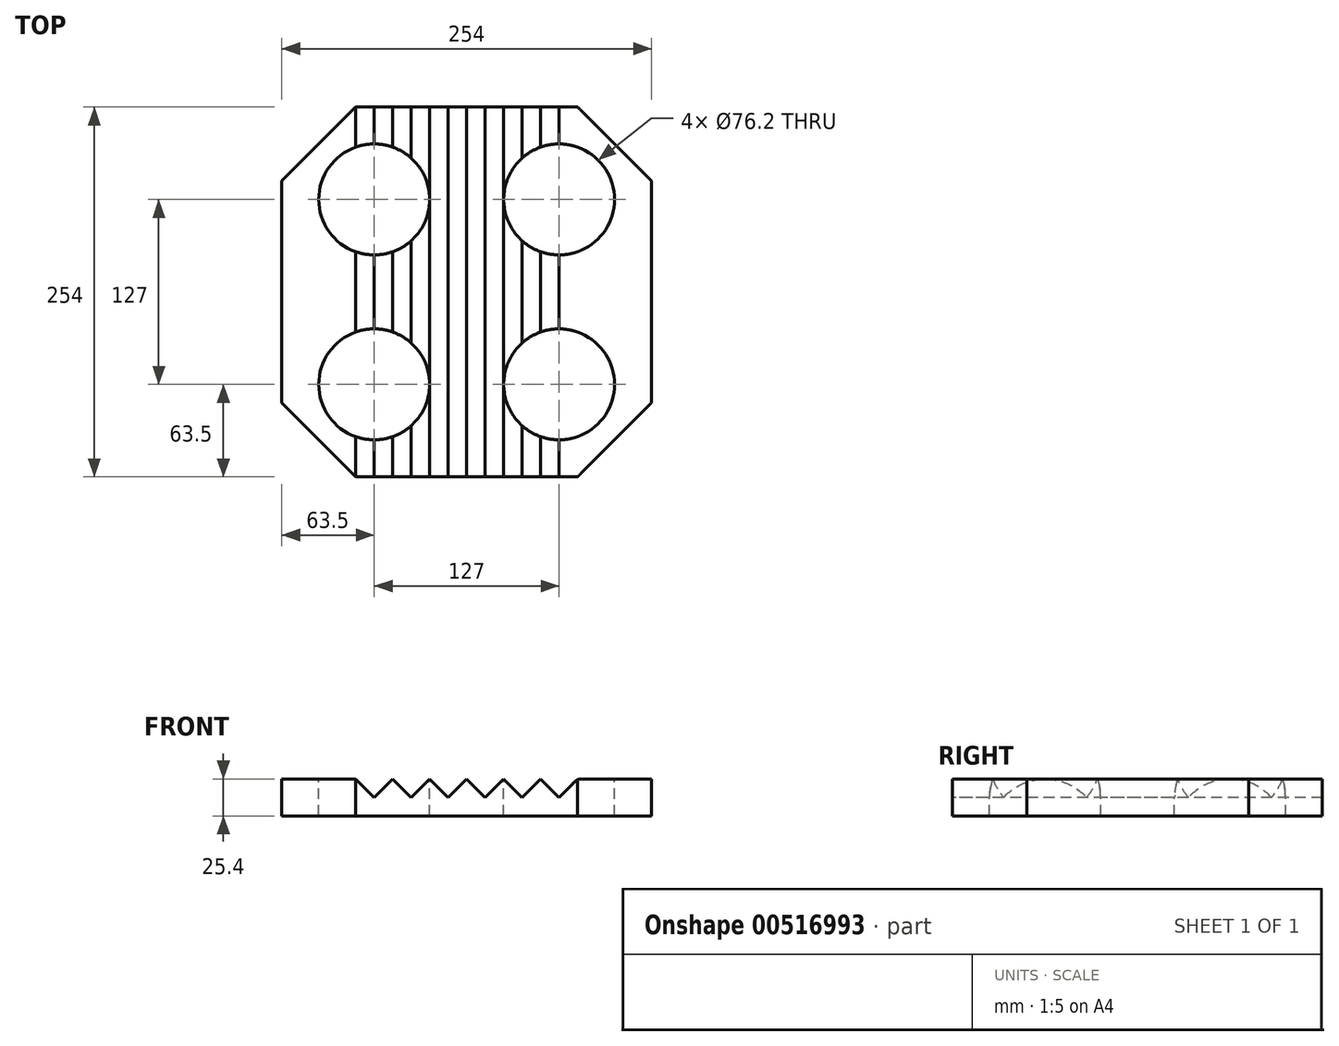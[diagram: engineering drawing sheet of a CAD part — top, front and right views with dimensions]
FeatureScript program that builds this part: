
annotation { "Feature Type Name" : "Feature", "Feature Type Description" : "" }
export const myFeature = defineFeature(function(context is Context, id is Id, definition is map)
    precondition{}
    {
        {
            var Q0;
            Q0=qCreatedBy(makeId("Top.planeOp"),FACE);
            var sketch = newSketch(context, id + "F0", { "sketchPlane" : qUnion([Q0])});
            skLineSegment(sketch, "E0.bottom", {"start": v(-127, 127) * mm, "end": v(127, 127) * mm});
            skLineSegment(sketch, "E0.top", {"start": v(-127, -127) * mm, "end": v(127, -127) * mm});
            skLineSegment(sketch, "E0.left", {"start": v(-127, 127) * mm, "end": v(-127, -127) * mm});
            skLineSegment(sketch, "E0.right", {"start": v(127, 127) * mm, "end": v(127, -127) * mm});
            skLineSegment(sketch, "E1", {"start": v(-127, 127) * mm, "end": v(127, -127) * mm, "construction": true});
            skLineSegment(sketch, "E2", {"start": v(127, 127) * mm, "end": v(-127, -127) * mm, "construction": true});
            skSolve(sketch);
        }
        {
            var Q0;
            Q0 = qSketchRegion(id + "F0", true);
            extrude(context, id + "F1", {"entities" : qUnion([Q0]), "depth" : 25.4 * mm, "offsetDistance" : 25.4 * mm});
        }
        {
            var Q0;
            Q0=makeQuery(id+"F1.opExtrude","CAP_FACE",FACE,{"disambiguationData":[OSD([sQuery(id+"F0.wireOp",EDGE,"E0.bottom"),sQuery(id+"F0.wireOp",EDGE,"E0.top"),sQuery(id+"F0.wireOp",EDGE,"E0.left"),sQuery(id+"F0.wireOp",EDGE,"E0.right")])],"isStart":false});
            var sketch = newSketch(context, id + "F2", { "sketchPlane" : qUnion([Q0])});
            skPoint(sketch, "E3", {"position": v(-63.5, 63.5) * mm});
            skPoint(sketch, "E4", {"position": v(63.5, 63.5) * mm});
            skPoint(sketch, "E5", {"position": v(63.5, -63.5) * mm});
            skPoint(sketch, "E6", {"position": v(-63.5, -63.5) * mm});
            skLineSegment(sketch, "E7", {"start": v(-63.5, 63.5) * mm, "end": v(-63.5, -63.5) * mm, "construction": true});
            skLineSegment(sketch, "E8", {"start": v(63.5, -63.5) * mm, "end": v(63.5, 63.5) * mm, "construction": true});
            skLineSegment(sketch, "E9", {"start": v(63.5, 63.5) * mm, "end": v(-63.5, 63.5) * mm, "construction": true});
            skLineSegment(sketch, "E10", {"start": v(63.5, -63.5) * mm, "end": v(-63.5, -63.5) * mm, "construction": true});
            skSolve(sketch);
        }
        {
            var Q0;
            Q0=sQuery(id+"F2.wireOp",VERTEX,"E3");
            var Q1;
            Q1=sQuery(id+"F2.wireOp",VERTEX,"E4");
            var Q2;
            Q2=sQuery(id+"F2.wireOp",VERTEX,"E5");
            var Q3;
            Q3=sQuery(id+"F2.wireOp",VERTEX,"E6");
            var Q4;
            Q4=makeQuery(id+"F1.opExtrude","SWEPT_BODY",BODY,{"disambiguationData":[OSD([sQuery(id+"F0.wireOp",EDGE,"E0.bottom"),sQuery(id+"F0.wireOp",EDGE,"E0.top"),sQuery(id+"F0.wireOp",EDGE,"E0.left"),sQuery(id+"F0.wireOp",EDGE,"E0.right")])]});
            hole(context, id + "F3", {"style" : HoleStyle.SIMPLE, "endStyle" : HoleEndStyle.THROUGH, "holeDiameter" : 76.2 * mm, "isTappedThrough" : true, "tappedDepth" : 12.7 * mm, "tapClearance" : 3, "locations" : qUnion([Q0, Q1, Q2, Q3]), "scope" : qUnion([Q4])});
        }
        {
            var Q0;
            Q0=makeQuery(id+"F1.opExtrude","SWEPT_EDGE",EDGE,{"disambiguationData":[OSD([sQuery(id+"F0.wireOp",EDGE,"E0.bottom"),sQuery(id+"F0.wireOp",EDGE,"E0.right")])]});
            var Q1;
            Q1=makeQuery(id+"F1.opExtrude","SWEPT_EDGE",EDGE,{"disambiguationData":[OSD([sQuery(id+"F0.wireOp",EDGE,"E0.top"),sQuery(id+"F0.wireOp",EDGE,"E0.right")])]});
            var Q2;
            Q2=makeQuery(id+"F1.opExtrude","SWEPT_EDGE",EDGE,{"disambiguationData":[OSD([sQuery(id+"F0.wireOp",EDGE,"E0.top"),sQuery(id+"F0.wireOp",EDGE,"E0.left")])]});
            var Q3;
            Q3=makeQuery(id+"F1.opExtrude","SWEPT_EDGE",EDGE,{"disambiguationData":[OSD([sQuery(id+"F0.wireOp",EDGE,"E0.bottom"),sQuery(id+"F0.wireOp",EDGE,"E0.left")])]});
            chamfer(context, id + "F4", {"entities" : qUnion([Q0, Q1, Q2, Q3]), "width" : 50.8 * mm, "tangentPropagation" : true});
        }
        {
            var Q0;
            Q0=makeQuery(id+"F1.opExtrude","SWEPT_FACE",FACE,{"disambiguationData":[OSD([sQuery(id+"F0.wireOp",EDGE,"E0.top")])]});
            var sketch = newSketch(context, id + "F5", { "sketchPlane" : qUnion([Q0])});
            skLineSegment(sketch, "E11", {"start": v(-76.2, 12.7) * mm, "end": v(76.2, 12.7) * mm, "construction": true});
            skLineSegment(sketch, "E12", {"start": v(-76.2, 25.4) * mm, "end": v(-63.5, 12.7) * mm});
            skLineSegment(sketch, "E13", {"start": v(-63.5, 12.7) * mm, "end": v(-50.8, 25.4) * mm});
            skLineSegment(sketch, "E14", {"start": v(-50.8, 25.4) * mm, "end": v(-38.1, 12.7) * mm});
            skLineSegment(sketch, "E15", {"start": v(-38.1, 12.7) * mm, "end": v(-25.4, 25.4) * mm});
            skLineSegment(sketch, "E16", {"start": v(-25.4, 25.4) * mm, "end": v(-12.7, 12.7) * mm});
            skLineSegment(sketch, "E17", {"start": v(-12.7, 12.7) * mm, "end": v(0, 25.4) * mm});
            skLineSegment(sketch, "E18", {"start": v(0, 25.4) * mm, "end": v(12.7, 12.7) * mm});
            skLineSegment(sketch, "E19", {"start": v(12.7, 12.7) * mm, "end": v(25.4, 25.4) * mm});
            skLineSegment(sketch, "E20", {"start": v(25.4, 25.4) * mm, "end": v(38.1, 12.7) * mm});
            skLineSegment(sketch, "E21", {"start": v(38.1, 12.7) * mm, "end": v(50.8, 25.4) * mm});
            skLineSegment(sketch, "E22", {"start": v(50.8, 25.4) * mm, "end": v(63.5, 12.7) * mm});
            skLineSegment(sketch, "E23", {"start": v(63.5, 12.7) * mm, "end": v(76.2, 25.4) * mm});
            skLineSegment(sketch, "E24", {"start": v(-76.2, 25.4) * mm, "end": v(76.2, 25.4) * mm});
            skSolve(sketch);
        }
        {
            var Q0;
            {var subQ0=sQuery(id+"F5.wireOp",EDGE,"E12");Q0=makeQuery(id+"F5.imprint","IMPRINT",FACE,{"disambiguationData":[TD([[makeQuery(id+"F5.imprint","IMPRINT",EDGE,{"derivedFrom":subQ0}),1.0]])]});}
            var Q1;
            {var subQ0=sQuery(id+"F5.wireOp",EDGE,"E14");Q1=makeQuery(id+"F5.imprint","IMPRINT",FACE,{"disambiguationData":[TD([[makeQuery(id+"F5.imprint","IMPRINT",EDGE,{"derivedFrom":subQ0}),1.0]])]});}
            var Q2;
            {var subQ0=sQuery(id+"F5.wireOp",EDGE,"E16");Q2=makeQuery(id+"F5.imprint","IMPRINT",FACE,{"disambiguationData":[TD([[makeQuery(id+"F5.imprint","IMPRINT",EDGE,{"derivedFrom":subQ0}),1.0]])]});}
            var Q3;
            {var subQ0=sQuery(id+"F5.wireOp",EDGE,"E18");Q3=makeQuery(id+"F5.imprint","IMPRINT",FACE,{"disambiguationData":[TD([[makeQuery(id+"F5.imprint","IMPRINT",EDGE,{"derivedFrom":subQ0}),1.0]])]});}
            var Q4;
            {var subQ0=sQuery(id+"F5.wireOp",EDGE,"E20");Q4=makeQuery(id+"F5.imprint","IMPRINT",FACE,{"disambiguationData":[TD([[makeQuery(id+"F5.imprint","IMPRINT",EDGE,{"derivedFrom":subQ0}),1.0]])]});}
            var Q5;
            {var subQ0=sQuery(id+"F5.wireOp",EDGE,"E22");Q5=makeQuery(id+"F5.imprint","IMPRINT",FACE,{"disambiguationData":[TD([[makeQuery(id+"F5.imprint","IMPRINT",EDGE,{"derivedFrom":subQ0}),1.0]])]});}
            extrude(context, id + "F6", {"entities" : qUnion([Q0, Q1, Q2, Q3, Q4, Q5]), "operationType" : NewBodyOperationType.REMOVE, "endBound" : BoundingType.THROUGH_ALL, "oppositeDirection" : true, "depth" : 25.4 * mm, "offsetDistance" : 25.4 * mm});
        }
        {
            var Q0;
            {var subQ0=sQuery(id+"F0.wireOp",EDGE,"E0.left");var subQ1=sQuery(id+"F0.wireOp",EDGE,"E0.top");var subQ2=sQuery(id+"F5.wireOp",EDGE,"E12");Q0=makeQuery(id+"F6.boolean.opBoolean","COPY",EDGE,{"disambiguationData":[TD([makeQuery(id+"F1.opExtrude","CAP_FACE",FACE,{"disambiguationData":[OSD([sQuery(id+"F0.wireOp",EDGE,"E0.bottom"),subQ1,subQ0,sQuery(id+"F0.wireOp",EDGE,"E0.right")])],"isStart":false}),makeQuery(id+"F1.opExtrude","SWEPT_FACE",FACE,{"disambiguationData":[OSD([subQ1])]}),makeQuery(id+"F3.hole-3.boolean.opBoolean","COPY",FACE,{"derivedFrom":makeQuery(id+"F3.hole-3.opRevolve","SWEPT_FACE",FACE,{"disambiguationData":[OSD([sQuery(id+"F3.hole-3.sketch.wireOp",EDGE,"core_line_2")])]})}),makeQuery(id+"F4.opChamfer","BLEND_FACE",FACE,{"disambiguationData":[OSD([subQ1,subQ0])]}),makeQuery(id+"F6.opExtrude","SWEPT_FACE",FACE,{"disambiguationData":[OSD([subQ2])]})])],"derivedFrom":makeQuery(id+"F6.opExtrude","SWEPT_EDGE",EDGE,{"disambiguationData":[OSD([subQ1,subQ0,subQ2,sQuery(id+"F5.wireOp",EDGE,"E24")])]})});}
            var Q1;
            {var subQ0=sQuery(id+"F5.wireOp",EDGE,"E24");var subQ1=sQuery(id+"F5.wireOp",EDGE,"E14");var subQ2=sQuery(id+"F5.wireOp",EDGE,"E13");Q1=makeQuery(id+"F6.boolean.opBoolean","TWEAK_EDGE",EDGE,{"disambiguationData":[OD(0.0)],"derivedFrom":[makeQuery(id+"F6.opExtrude","SWEPT_EDGE",EDGE,{"disambiguationData":[OSD([subQ2,subQ1,subQ0]),OD(0.0)]}),makeQuery(id+"F6.opExtrude","SWEPT_EDGE",EDGE,{"disambiguationData":[OSD([subQ2,subQ1,subQ0]),OD(1.0)]})]});}
            var Q2;
            {var subQ0=sQuery(id+"F5.wireOp",EDGE,"E24");var subQ1=sQuery(id+"F5.wireOp",EDGE,"E14");var subQ2=sQuery(id+"F5.wireOp",EDGE,"E13");Q2=makeQuery(id+"F6.boolean.opBoolean","TWEAK_EDGE",EDGE,{"disambiguationData":[OD(1.0)],"derivedFrom":[makeQuery(id+"F6.opExtrude","SWEPT_EDGE",EDGE,{"disambiguationData":[OSD([subQ2,subQ1,subQ0]),OD(0.0)]}),makeQuery(id+"F6.opExtrude","SWEPT_EDGE",EDGE,{"disambiguationData":[OSD([subQ2,subQ1,subQ0]),OD(1.0)]})]});}
            var Q3;
            {var subQ0=sQuery(id+"F5.wireOp",EDGE,"E24");var subQ1=sQuery(id+"F5.wireOp",EDGE,"E16");var subQ2=sQuery(id+"F5.wireOp",EDGE,"E15");Q3=makeQuery(id+"F6.boolean.opBoolean","TWEAK_EDGE",EDGE,{"disambiguationData":[OD(2.0)],"derivedFrom":[makeQuery(id+"F6.opExtrude","SWEPT_EDGE",EDGE,{"disambiguationData":[OSD([subQ2,subQ1,subQ0]),OD(0.0)]}),makeQuery(id+"F6.opExtrude","SWEPT_EDGE",EDGE,{"disambiguationData":[OSD([subQ2,subQ1,subQ0]),OD(1.0)]})]});}
            var Q4;
            {var subQ0=sQuery(id+"F5.wireOp",EDGE,"E24");var subQ1=sQuery(id+"F5.wireOp",EDGE,"E16");var subQ2=sQuery(id+"F5.wireOp",EDGE,"E15");Q4=makeQuery(id+"F6.boolean.opBoolean","TWEAK_EDGE",EDGE,{"disambiguationData":[OD(0.0)],"derivedFrom":[makeQuery(id+"F6.opExtrude","SWEPT_EDGE",EDGE,{"disambiguationData":[OSD([subQ2,subQ1,subQ0]),OD(0.0)]}),makeQuery(id+"F6.opExtrude","SWEPT_EDGE",EDGE,{"disambiguationData":[OSD([subQ2,subQ1,subQ0]),OD(1.0)]})]});}
            var Q5;
            {var subQ0=sQuery(id+"F5.wireOp",EDGE,"E24");var subQ1=sQuery(id+"F5.wireOp",EDGE,"E18");var subQ2=sQuery(id+"F5.wireOp",EDGE,"E17");Q5=makeQuery(id+"F6.boolean.opBoolean","TWEAK_EDGE",EDGE,{"derivedFrom":[makeQuery(id+"F6.opExtrude","SWEPT_EDGE",EDGE,{"disambiguationData":[OSD([subQ2,subQ1,subQ0]),OD(0.0)]}),makeQuery(id+"F6.opExtrude","SWEPT_EDGE",EDGE,{"disambiguationData":[OSD([subQ2,subQ1,subQ0]),OD(1.0)]})]});}
            var Q6;
            {var subQ0=sQuery(id+"F5.wireOp",EDGE,"E24");var subQ1=sQuery(id+"F5.wireOp",EDGE,"E20");var subQ2=sQuery(id+"F5.wireOp",EDGE,"E19");Q6=makeQuery(id+"F6.boolean.opBoolean","TWEAK_EDGE",EDGE,{"disambiguationData":[OD(0.0)],"derivedFrom":[makeQuery(id+"F6.opExtrude","SWEPT_EDGE",EDGE,{"disambiguationData":[OSD([subQ2,subQ1,subQ0]),OD(0.0)]}),makeQuery(id+"F6.opExtrude","SWEPT_EDGE",EDGE,{"disambiguationData":[OSD([subQ2,subQ1,subQ0]),OD(1.0)]})]});}
            var Q7;
            {var subQ0=sQuery(id+"F0.wireOp",EDGE,"E0.left");var subQ1=sQuery(id+"F0.wireOp",EDGE,"E0.top");var subQ2=sQuery(id+"F5.wireOp",EDGE,"E12");Q7=makeQuery(id+"F6.boolean.opBoolean","COPY",EDGE,{"disambiguationData":[TD([makeQuery(id+"F1.opExtrude","CAP_FACE",FACE,{"disambiguationData":[OSD([sQuery(id+"F0.wireOp",EDGE,"E0.bottom"),subQ1,subQ0,sQuery(id+"F0.wireOp",EDGE,"E0.right")])],"isStart":false}),makeQuery(id+"F3.hole-0.boolean.opBoolean","COPY",FACE,{"derivedFrom":makeQuery(id+"F3.hole-0.opRevolve","SWEPT_FACE",FACE,{"disambiguationData":[OSD([sQuery(id+"F3.hole-0.sketch.wireOp",EDGE,"core_line_2")])]})}),makeQuery(id+"F3.hole-3.boolean.opBoolean","COPY",FACE,{"derivedFrom":makeQuery(id+"F3.hole-3.opRevolve","SWEPT_FACE",FACE,{"disambiguationData":[OSD([sQuery(id+"F3.hole-3.sketch.wireOp",EDGE,"core_line_2")])]})}),makeQuery(id+"F6.opExtrude","SWEPT_FACE",FACE,{"disambiguationData":[OSD([subQ2])]})])],"derivedFrom":makeQuery(id+"F6.opExtrude","SWEPT_EDGE",EDGE,{"disambiguationData":[OSD([subQ1,subQ0,subQ2,sQuery(id+"F5.wireOp",EDGE,"E24")])]})});}
            var Q8;
            {var subQ0=sQuery(id+"F0.wireOp",EDGE,"E0.left");var subQ1=sQuery(id+"F0.wireOp",EDGE,"E0.bottom");var subQ2=sQuery(id+"F0.wireOp",EDGE,"E0.top");var subQ3=sQuery(id+"F5.wireOp",EDGE,"E12");Q8=makeQuery(id+"F6.boolean.opBoolean","COPY",EDGE,{"disambiguationData":[TD([makeQuery(id+"F1.opExtrude","SWEPT_FACE",FACE,{"disambiguationData":[OSD([subQ1])]}),makeQuery(id+"F1.opExtrude","CAP_FACE",FACE,{"disambiguationData":[OSD([subQ1,subQ2,subQ0,sQuery(id+"F0.wireOp",EDGE,"E0.right")])],"isStart":false}),makeQuery(id+"F3.hole-0.boolean.opBoolean","COPY",FACE,{"derivedFrom":makeQuery(id+"F3.hole-0.opRevolve","SWEPT_FACE",FACE,{"disambiguationData":[OSD([sQuery(id+"F3.hole-0.sketch.wireOp",EDGE,"core_line_2")])]})}),makeQuery(id+"F4.opChamfer","BLEND_FACE",FACE,{"disambiguationData":[OSD([subQ1,subQ0])]}),makeQuery(id+"F6.opExtrude","SWEPT_FACE",FACE,{"disambiguationData":[OSD([subQ3])]})])],"derivedFrom":makeQuery(id+"F6.opExtrude","SWEPT_EDGE",EDGE,{"disambiguationData":[OSD([subQ2,subQ0,subQ3,sQuery(id+"F5.wireOp",EDGE,"E24")])]})});}
            var Q9;
            {var subQ0=sQuery(id+"F5.wireOp",EDGE,"E24");var subQ1=sQuery(id+"F5.wireOp",EDGE,"E14");var subQ2=sQuery(id+"F5.wireOp",EDGE,"E13");Q9=makeQuery(id+"F6.boolean.opBoolean","TWEAK_EDGE",EDGE,{"disambiguationData":[OD(2.0)],"derivedFrom":[makeQuery(id+"F6.opExtrude","SWEPT_EDGE",EDGE,{"disambiguationData":[OSD([subQ2,subQ1,subQ0]),OD(0.0)]}),makeQuery(id+"F6.opExtrude","SWEPT_EDGE",EDGE,{"disambiguationData":[OSD([subQ2,subQ1,subQ0]),OD(1.0)]})]});}
            var Q10;
            {var subQ0=sQuery(id+"F5.wireOp",EDGE,"E24");var subQ1=sQuery(id+"F5.wireOp",EDGE,"E22");var subQ2=sQuery(id+"F5.wireOp",EDGE,"E21");Q10=makeQuery(id+"F6.boolean.opBoolean","TWEAK_EDGE",EDGE,{"disambiguationData":[OD(2.0)],"derivedFrom":[makeQuery(id+"F6.opExtrude","SWEPT_EDGE",EDGE,{"disambiguationData":[OSD([subQ2,subQ1,subQ0]),OD(0.0)]}),makeQuery(id+"F6.opExtrude","SWEPT_EDGE",EDGE,{"disambiguationData":[OSD([subQ2,subQ1,subQ0]),OD(1.0)]})]});}
            var Q11;
            {var subQ0=sQuery(id+"F5.wireOp",EDGE,"E24");var subQ1=sQuery(id+"F5.wireOp",EDGE,"E22");var subQ2=sQuery(id+"F5.wireOp",EDGE,"E21");Q11=makeQuery(id+"F6.boolean.opBoolean","TWEAK_EDGE",EDGE,{"disambiguationData":[OD(1.0)],"derivedFrom":[makeQuery(id+"F6.opExtrude","SWEPT_EDGE",EDGE,{"disambiguationData":[OSD([subQ2,subQ1,subQ0]),OD(0.0)]}),makeQuery(id+"F6.opExtrude","SWEPT_EDGE",EDGE,{"disambiguationData":[OSD([subQ2,subQ1,subQ0]),OD(1.0)]})]});}
            var Q12;
            {var subQ0=sQuery(id+"F0.wireOp",EDGE,"E0.right");var subQ1=sQuery(id+"F0.wireOp",EDGE,"E0.top");var subQ2=sQuery(id+"F5.wireOp",EDGE,"E23");Q12=makeQuery(id+"F6.boolean.opBoolean","COPY",EDGE,{"disambiguationData":[TD([makeQuery(id+"F1.opExtrude","CAP_FACE",FACE,{"disambiguationData":[OSD([sQuery(id+"F0.wireOp",EDGE,"E0.bottom"),subQ1,sQuery(id+"F0.wireOp",EDGE,"E0.left"),subQ0])],"isStart":false}),makeQuery(id+"F1.opExtrude","SWEPT_FACE",FACE,{"disambiguationData":[OSD([subQ1])]}),makeQuery(id+"F3.hole-2.boolean.opBoolean","COPY",FACE,{"derivedFrom":makeQuery(id+"F3.hole-2.opRevolve","SWEPT_FACE",FACE,{"disambiguationData":[OSD([sQuery(id+"F3.hole-2.sketch.wireOp",EDGE,"core_line_2")])]})}),makeQuery(id+"F4.opChamfer","BLEND_FACE",FACE,{"disambiguationData":[OSD([subQ1,subQ0])]}),makeQuery(id+"F6.opExtrude","SWEPT_FACE",FACE,{"disambiguationData":[OSD([subQ2])]})])],"derivedFrom":makeQuery(id+"F6.opExtrude","SWEPT_EDGE",EDGE,{"disambiguationData":[OSD([subQ1,subQ0,subQ2,sQuery(id+"F5.wireOp",EDGE,"E24")])]})});}
            var Q13;
            {var subQ0=sQuery(id+"F5.wireOp",EDGE,"E24");var subQ1=sQuery(id+"F5.wireOp",EDGE,"E22");var subQ2=sQuery(id+"F5.wireOp",EDGE,"E21");Q13=makeQuery(id+"F6.boolean.opBoolean","TWEAK_EDGE",EDGE,{"disambiguationData":[OD(0.0)],"derivedFrom":[makeQuery(id+"F6.opExtrude","SWEPT_EDGE",EDGE,{"disambiguationData":[OSD([subQ2,subQ1,subQ0]),OD(0.0)]}),makeQuery(id+"F6.opExtrude","SWEPT_EDGE",EDGE,{"disambiguationData":[OSD([subQ2,subQ1,subQ0]),OD(1.0)]})]});}
            var Q14;
            {var subQ0=sQuery(id+"F5.wireOp",EDGE,"E24");var subQ1=sQuery(id+"F5.wireOp",EDGE,"E16");var subQ2=sQuery(id+"F5.wireOp",EDGE,"E15");Q14=makeQuery(id+"F6.boolean.opBoolean","TWEAK_EDGE",EDGE,{"disambiguationData":[OD(1.0)],"derivedFrom":[makeQuery(id+"F6.opExtrude","SWEPT_EDGE",EDGE,{"disambiguationData":[OSD([subQ2,subQ1,subQ0]),OD(0.0)]}),makeQuery(id+"F6.opExtrude","SWEPT_EDGE",EDGE,{"disambiguationData":[OSD([subQ2,subQ1,subQ0]),OD(1.0)]})]});}
            var Q15;
            {var subQ0=sQuery(id+"F0.wireOp",EDGE,"E0.right");var subQ1=sQuery(id+"F0.wireOp",EDGE,"E0.bottom");var subQ2=sQuery(id+"F0.wireOp",EDGE,"E0.top");var subQ3=sQuery(id+"F5.wireOp",EDGE,"E23");Q15=makeQuery(id+"F6.boolean.opBoolean","COPY",EDGE,{"disambiguationData":[TD([makeQuery(id+"F1.opExtrude","SWEPT_FACE",FACE,{"disambiguationData":[OSD([subQ1])]}),makeQuery(id+"F1.opExtrude","CAP_FACE",FACE,{"disambiguationData":[OSD([subQ1,subQ2,sQuery(id+"F0.wireOp",EDGE,"E0.left"),subQ0])],"isStart":false}),makeQuery(id+"F3.hole-1.boolean.opBoolean","COPY",FACE,{"derivedFrom":makeQuery(id+"F3.hole-1.opRevolve","SWEPT_FACE",FACE,{"disambiguationData":[OSD([sQuery(id+"F3.hole-1.sketch.wireOp",EDGE,"core_line_2")])]})}),makeQuery(id+"F4.opChamfer","BLEND_FACE",FACE,{"disambiguationData":[OSD([subQ1,subQ0])]}),makeQuery(id+"F6.opExtrude","SWEPT_FACE",FACE,{"disambiguationData":[OSD([subQ3])]})])],"derivedFrom":makeQuery(id+"F6.opExtrude","SWEPT_EDGE",EDGE,{"disambiguationData":[OSD([subQ2,subQ0,subQ3,sQuery(id+"F5.wireOp",EDGE,"E24")])]})});}
            var Q16;
            {var subQ0=sQuery(id+"F0.wireOp",EDGE,"E0.right");var subQ1=sQuery(id+"F0.wireOp",EDGE,"E0.top");var subQ2=sQuery(id+"F5.wireOp",EDGE,"E23");Q16=makeQuery(id+"F6.boolean.opBoolean","COPY",EDGE,{"disambiguationData":[TD([makeQuery(id+"F1.opExtrude","CAP_FACE",FACE,{"disambiguationData":[OSD([sQuery(id+"F0.wireOp",EDGE,"E0.bottom"),subQ1,sQuery(id+"F0.wireOp",EDGE,"E0.left"),subQ0])],"isStart":false}),makeQuery(id+"F3.hole-1.boolean.opBoolean","COPY",FACE,{"derivedFrom":makeQuery(id+"F3.hole-1.opRevolve","SWEPT_FACE",FACE,{"disambiguationData":[OSD([sQuery(id+"F3.hole-1.sketch.wireOp",EDGE,"core_line_2")])]})}),makeQuery(id+"F3.hole-2.boolean.opBoolean","COPY",FACE,{"derivedFrom":makeQuery(id+"F3.hole-2.opRevolve","SWEPT_FACE",FACE,{"disambiguationData":[OSD([sQuery(id+"F3.hole-2.sketch.wireOp",EDGE,"core_line_2")])]})}),makeQuery(id+"F6.opExtrude","SWEPT_FACE",FACE,{"disambiguationData":[OSD([subQ2])]})])],"derivedFrom":makeQuery(id+"F6.opExtrude","SWEPT_EDGE",EDGE,{"disambiguationData":[OSD([subQ1,subQ0,subQ2,sQuery(id+"F5.wireOp",EDGE,"E24")])]})});}
            fillet(context, id + "F7", {"entities" : qUnion([Q0, Q1, Q2, Q3, Q4, Q5, Q6, Q7, Q8, Q9, Q10, Q11, Q12, Q13, Q14, Q15, Q16]), "radius" : 6.35 * mm, "tangentPropagation" : true, "allowEdgeOverflow" : false});
        }
    });
